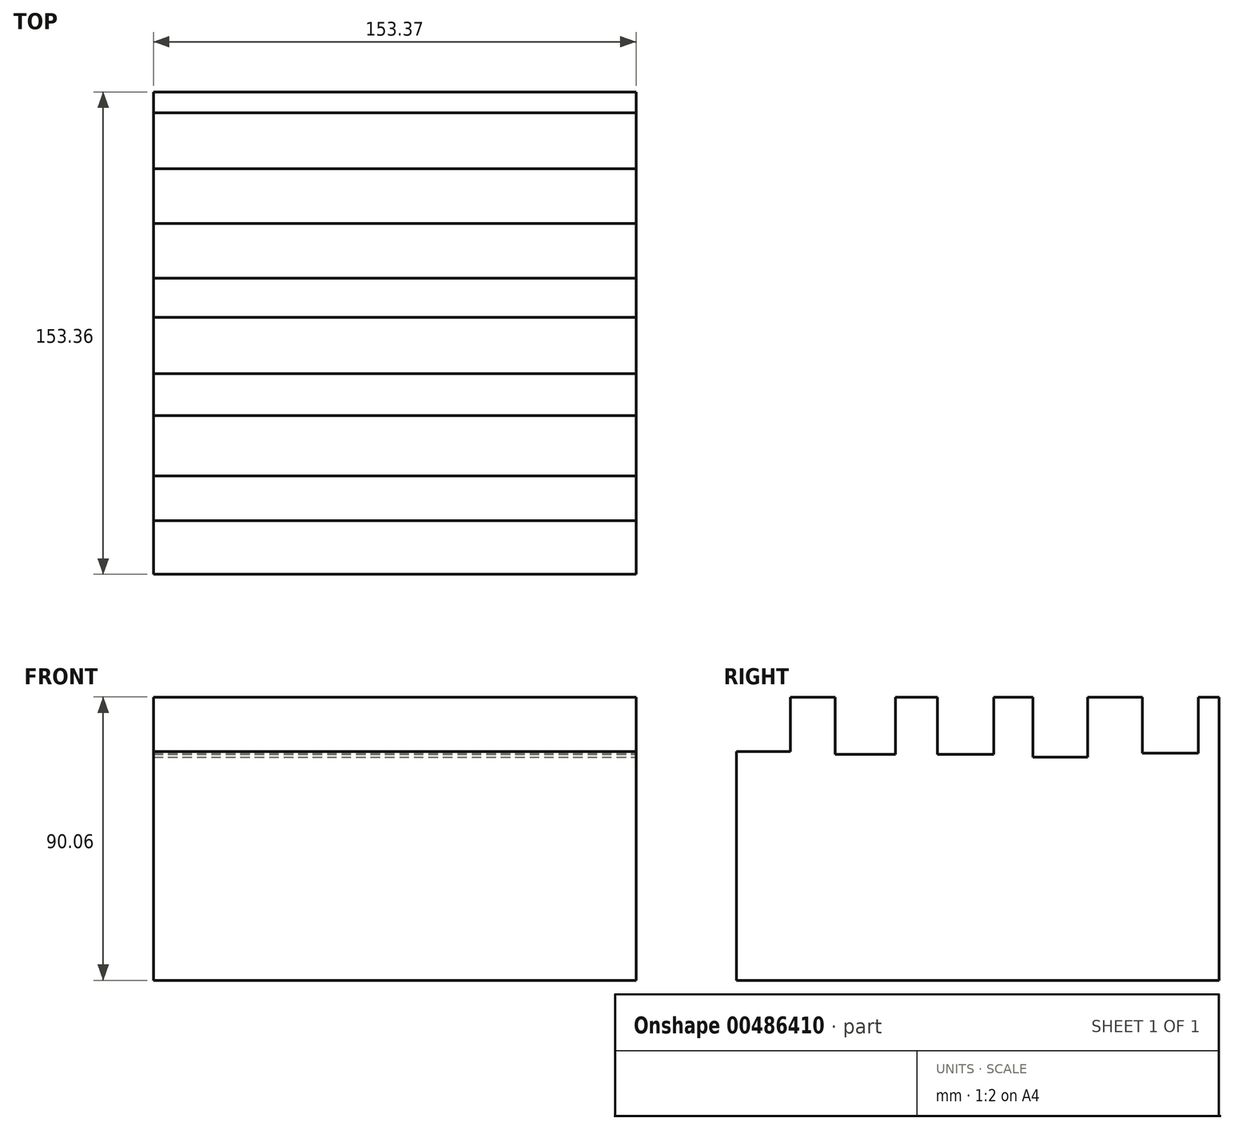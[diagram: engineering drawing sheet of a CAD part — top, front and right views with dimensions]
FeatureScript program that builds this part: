
annotation { "Feature Type Name" : "Feature", "Feature Type Description" : "" }
export const myFeature = defineFeature(function(context is Context, id is Id, definition is map)
    precondition{}
    {
        {
            var Q0;
            Q0=qCreatedBy(makeId("Front.planeOp"),FACE);
            var sketch = newSketch(context, id + "F0", { "sketchPlane" : qUnion([Q0])});
            skLineSegment(sketch, "E0.bottom", {"start": v(-76.24, 32.55) * mm, "end": v(77.13, 32.55) * mm});
            skLineSegment(sketch, "E0.top", {"start": v(-76.24, -57.51) * mm, "end": v(77.13, -57.51) * mm});
            skLineSegment(sketch, "E0.left", {"start": v(-76.24, 32.55) * mm, "end": v(-76.24, -57.51) * mm});
            skLineSegment(sketch, "E0.right", {"start": v(77.13, 32.55) * mm, "end": v(77.13, -57.51) * mm});
            skSolve(sketch);
        }
        {
            var Q0;
            Q0=makeQuery(id+"F0.imprint","IMPRINT",FACE,{"disambiguationData":[TD([[makeQuery(id+"F0.imprint","IMPRINT",EDGE,{"derivedFrom":sQuery(id+"F0.wireOp",EDGE,"E0.bottom")}),-1.0]])]});
            extrude(context, id + "F1", {"entities" : qUnion([Q0]), "endBound" : BoundingType.SYMMETRIC, "depth" : 153.37 * mm});
        }
        {
            var Q0;
            Q0=makeQuery(id+"F1.opExtrude","SWEPT_FACE",FACE,{"disambiguationData":[OSD([sQuery(id+"F0.wireOp",EDGE,"E0.right")])]});
            var sketch = newSketch(context, id + "F2", { "sketchPlane" : qUnion([Q0])});
            skLineSegment(sketch, "E1.bottom", {"start": v(-76.68, 32.55) * mm, "end": v(-59.65, 32.55) * mm});
            skLineSegment(sketch, "E1.top", {"start": v(-76.68, 15.16) * mm, "end": v(-59.65, 15.16) * mm});
            skLineSegment(sketch, "E1.left", {"start": v(-76.68, 32.55) * mm, "end": v(-76.68, 15.16) * mm});
            skLineSegment(sketch, "E1.right", {"start": v(-59.65, 32.55) * mm, "end": v(-59.65, 15.16) * mm});
            skLineSegment(sketch, "E2.bottom", {"start": v(-45.38, 32.55) * mm, "end": v(-26.2, 32.55) * mm});
            skLineSegment(sketch, "E2.top", {"start": v(-45.38, 14.27) * mm, "end": v(-26.2, 14.27) * mm});
            skLineSegment(sketch, "E2.left", {"start": v(-45.38, 32.55) * mm, "end": v(-45.38, 14.27) * mm});
            skLineSegment(sketch, "E2.right", {"start": v(-26.2, 32.55) * mm, "end": v(-26.2, 14.27) * mm});
            skLineSegment(sketch, "E3.bottom", {"start": v(-12.83, 32.55) * mm, "end": v(5, 32.55) * mm});
            skLineSegment(sketch, "E3.top", {"start": v(-12.83, 14.27) * mm, "end": v(5, 14.27) * mm});
            skLineSegment(sketch, "E3.left", {"start": v(-12.83, 32.55) * mm, "end": v(-12.83, 14.27) * mm});
            skLineSegment(sketch, "E3.right", {"start": v(5, 32.55) * mm, "end": v(5, 14.27) * mm});
            skLineSegment(sketch, "E4.bottom", {"start": v(17.48, 32.55) * mm, "end": v(34.87, 32.55) * mm});
            skLineSegment(sketch, "E4.top", {"start": v(17.48, 13.37) * mm, "end": v(34.87, 13.37) * mm});
            skLineSegment(sketch, "E4.left", {"start": v(17.48, 32.55) * mm, "end": v(17.48, 13.37) * mm});
            skLineSegment(sketch, "E4.right", {"start": v(34.87, 32.55) * mm, "end": v(34.87, 13.37) * mm});
            skLineSegment(sketch, "E5.bottom", {"start": v(52.26, 32.55) * mm, "end": v(70.09, 32.55) * mm});
            skLineSegment(sketch, "E5.top", {"start": v(52.26, 14.71) * mm, "end": v(70.09, 14.71) * mm});
            skLineSegment(sketch, "E5.left", {"start": v(52.26, 32.55) * mm, "end": v(52.26, 14.71) * mm});
            skLineSegment(sketch, "E5.right", {"start": v(70.09, 32.55) * mm, "end": v(70.09, 14.71) * mm});
            skSolve(sketch);
        }
        {
            var Q0;
            Q0=makeQuery(id+"F2.imprint","IMPRINT",FACE,{"disambiguationData":[TD([[makeQuery(id+"F2.imprint","IMPRINT",EDGE,{"derivedFrom":sQuery(id+"F2.wireOp",EDGE,"E1.bottom")}),-1.0]])]});
            var Q1;
            Q1=makeQuery(id+"F2.imprint","IMPRINT",FACE,{"disambiguationData":[TD([[makeQuery(id+"F2.imprint","IMPRINT",EDGE,{"derivedFrom":sQuery(id+"F2.wireOp",EDGE,"E2.bottom")}),-1.0]])]});
            var Q2;
            Q2=makeQuery(id+"F2.imprint","IMPRINT",FACE,{"disambiguationData":[TD([[makeQuery(id+"F2.imprint","IMPRINT",EDGE,{"derivedFrom":sQuery(id+"F2.wireOp",EDGE,"E3.bottom")}),-1.0]])]});
            var Q3;
            Q3=makeQuery(id+"F2.imprint","IMPRINT",FACE,{"disambiguationData":[TD([[makeQuery(id+"F2.imprint","IMPRINT",EDGE,{"derivedFrom":sQuery(id+"F2.wireOp",EDGE,"E4.bottom")}),-1.0]])]});
            var Q4;
            Q4=makeQuery(id+"F2.imprint","IMPRINT",FACE,{"disambiguationData":[TD([[makeQuery(id+"F2.imprint","IMPRINT",EDGE,{"derivedFrom":sQuery(id+"F2.wireOp",EDGE,"E5.bottom")}),-1.0]])]});
            extrude(context, id + "F3", {"entities" : qUnion([Q0, Q1, Q2, Q3, Q4]), "operationType" : NewBodyOperationType.REMOVE, "oppositeDirection" : true, "depth" : 228.6 * mm});
        }
    });
